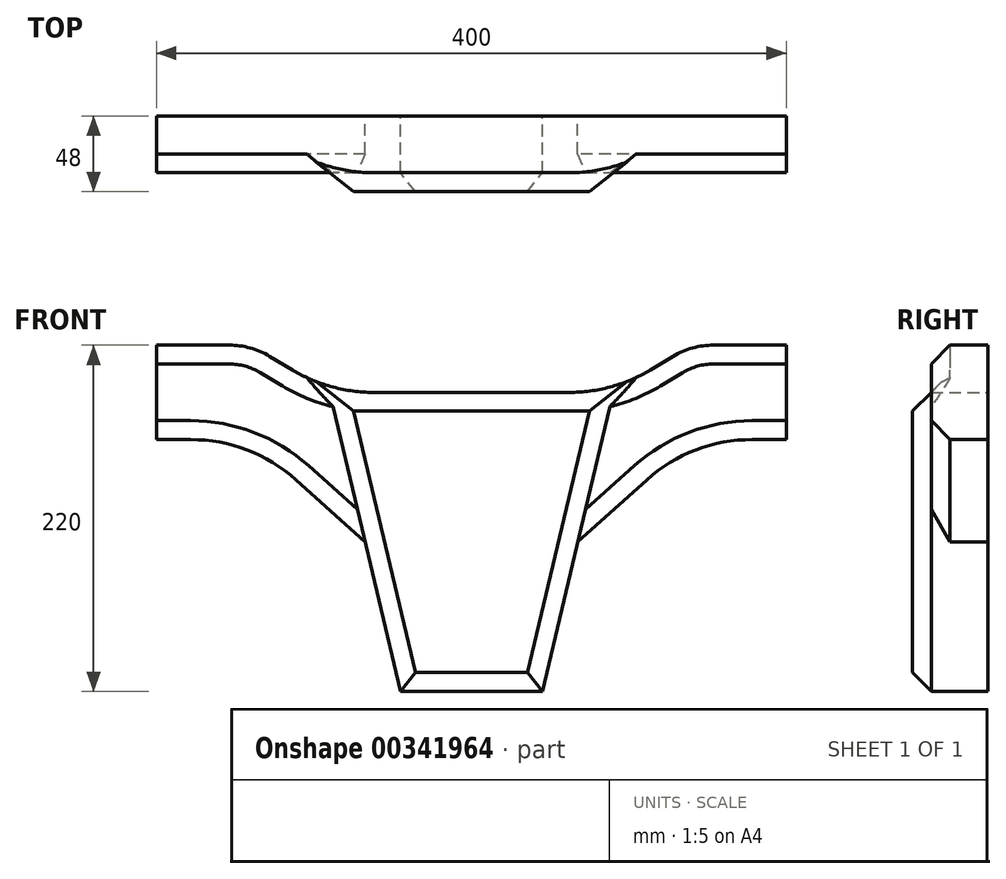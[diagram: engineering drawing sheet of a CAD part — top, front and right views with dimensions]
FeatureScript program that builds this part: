
annotation { "Feature Type Name" : "Feature", "Feature Type Description" : "" }
export const myFeature = defineFeature(function(context is Context, id is Id, definition is map)
    precondition{}
    {
        {
            var Q0;
            Q0=qCreatedBy(makeId("Front.planeOp"),FACE);
            var sketch = newSketch(context, id + "F0", { "sketchPlane" : qUnion([Q0])});
            skLineSegment(sketch, "E0", {"start": v(-45, -90) * mm, "end": v(45, -90) * mm});
            skLineSegment(sketch, "E1", {"start": v(-90, 100) * mm, "end": v(90, 100) * mm});
            skLineSegment(sketch, "E2", {"start": v(-45, -90) * mm, "end": v(-90, 100) * mm});
            skLineSegment(sketch, "E3", {"start": v(45, -90) * mm, "end": v(90, 100) * mm});
            skLineSegment(sketch, "E4", {"start": v(-200, 130) * mm, "end": v(-140, 130) * mm});
            skLineSegment(sketch, "E5", {"start": v(90, 100) * mm, "end": v(140, 130) * mm});
            skLineSegment(sketch, "E6.0", {"start": v(-200, 100) * mm, "end": v(200, 100) * mm, "construction": true});
            skLineSegment(sketch, "E7.0", {"start": v(-200, 70) * mm, "end": v(-140, 70) * mm});
            skLineSegment(sketch, "E8", {"start": v(67.5, 5) * mm, "end": v(140, 70) * mm});
            skLineSegment(sketch, "E9", {"start": v(-90, 100) * mm, "end": v(-140, 130) * mm});
            skLineSegment(sketch, "E10", {"start": v(-67.5, 5) * mm, "end": v(-140, 70) * mm});
            skLineSegment(sketch, "E11.trimOffspring", {"start": v(140, 70) * mm, "end": v(200, 70) * mm});
            skLineSegment(sketch, "E12", {"start": v(-200, 130) * mm, "end": v(-200, 70) * mm});
            skLineSegment(sketch, "E13", {"start": v(200, 130) * mm, "end": v(200, 70) * mm});
            skLineSegment(sketch, "E14.trimOffspring", {"start": v(140, 130) * mm, "end": v(200, 130) * mm});
            skSolve(sketch);
        }
        {
            var Q0;
            {var subQ3=sQuery(id+"F0.wireOp",EDGE,"E0");Q0=makeQuery(id+"F0.imprint","IMPRINT",FACE,{"disambiguationData":[TD([[makeQuery(id+"F0.imprint","IMPRINT",EDGE,{"derivedFrom":subQ3}),1.0]])]});}
            extrude(context, id + "F1", {"entities" : qUnion([Q0]), "depth" : 48 * mm});
        }
        {
            var Q0;
            {var subQ1=sQuery(id+"F0.wireOp",EDGE,"E5");Q0=makeQuery(id+"F0.imprint","IMPRINT",FACE,{"disambiguationData":[TD([[makeQuery(id+"F0.imprint","IMPRINT",EDGE,{"derivedFrom":subQ1}),-1.0]])]});}
            var Q1;
            Q1=makeQuery(id+"F0.imprint","IMPRINT",FACE,{"disambiguationData":[TD([[makeQuery(id+"F0.imprint","IMPRINT",EDGE,{"derivedFrom":sQuery(id+"F0.wireOp",EDGE,"E4")}),-1.0]])]});
            extrude(context, id + "F2", {"entities" : qUnion([Q0, Q1]), "operationType" : NewBodyOperationType.ADD, "depth" : 36 * mm});
        }
        {
            var Q0;
            {var subQ0=sQuery(id+"F0.wireOp",EDGE,"E9");var subQ1=sQuery(id+"F0.wireOp",EDGE,"E2");var subQ2=sQuery(id+"F0.wireOp",EDGE,"E1");Q0=makeQuery(id+"F2.boolean.opBoolean","MERGE",EDGE,{"derivedFrom":[makeQuery(id+"F1.opExtrude","SWEPT_EDGE",EDGE,{"disambiguationData":[OSD([subQ2,subQ1,subQ0])]}),makeQuery(id+"F2.opExtrude","SWEPT_EDGE",EDGE,{"disambiguationData":[OSD([subQ2,subQ1,subQ0])]})]});}
            var Q1;
            {var subQ0=sQuery(id+"F0.wireOp",EDGE,"E5");var subQ1=sQuery(id+"F0.wireOp",EDGE,"E3");var subQ2=sQuery(id+"F0.wireOp",EDGE,"E1");Q1=makeQuery(id+"F2.boolean.opBoolean","MERGE",EDGE,{"derivedFrom":[makeQuery(id+"F1.opExtrude","SWEPT_EDGE",EDGE,{"disambiguationData":[OSD([subQ2,subQ1,subQ0])]}),makeQuery(id+"F2.opExtrude","SWEPT_EDGE",EDGE,{"disambiguationData":[OSD([subQ2,subQ1,subQ0])]})]});}
            var Q2;
            Q2=makeQuery(id+"F2.opExtrude","SWEPT_EDGE",EDGE,{"disambiguationData":[OSD([sQuery(id+"F0.wireOp",EDGE,"E7.0"),sQuery(id+"F0.wireOp",EDGE,"E10")])]});
            var Q3;
            Q3=makeQuery(id+"F2.opExtrude","SWEPT_EDGE",EDGE,{"disambiguationData":[OSD([sQuery(id+"F0.wireOp",EDGE,"E8"),sQuery(id+"F0.wireOp",EDGE,"E11.trimOffspring")])]});
            fillet(context, id + "F3", {"entities" : qUnion([Q0, Q1, Q2, Q3]), "radius" : 100 * mm, "tangentPropagation" : true, "allowEdgeOverflow" : false});
        }
        {
            var Q0;
            Q0=makeQuery(id+"F2.opExtrude","SWEPT_EDGE",EDGE,{"disambiguationData":[OSD([sQuery(id+"F0.wireOp",EDGE,"E4"),sQuery(id+"F0.wireOp",EDGE,"E9")])]});
            var Q1;
            Q1=makeQuery(id+"F2.opExtrude","SWEPT_EDGE",EDGE,{"disambiguationData":[OSD([sQuery(id+"F0.wireOp",EDGE,"E5"),sQuery(id+"F0.wireOp",EDGE,"E14.trimOffspring")])]});
            fillet(context, id + "F4", {"entities" : qUnion([Q0, Q1]), "radius" : 50 * mm, "tangentPropagation" : true, "allowEdgeOverflow" : false});
        }
        {
            var Q0;
            Q0=makeQuery(id+"F1.opExtrude","CAP_EDGE",EDGE,{"disambiguationData":[OSD([sQuery(id+"F0.wireOp",EDGE,"E1")])],"isStart":false});
            var Q1;
            Q1=makeQuery(id+"F1.opExtrude","CAP_EDGE",EDGE,{"disambiguationData":[OSD([sQuery(id+"F0.wireOp",EDGE,"E2")])],"isStart":false});
            var Q2;
            Q2=makeQuery(id+"F1.opExtrude","CAP_EDGE",EDGE,{"disambiguationData":[OSD([sQuery(id+"F0.wireOp",EDGE,"E3")])],"isStart":false});
            var Q3;
            Q3=makeQuery(id+"F1.opExtrude","CAP_EDGE",EDGE,{"disambiguationData":[OSD([sQuery(id+"F0.wireOp",EDGE,"E0")])],"isStart":false});
            chamfer(context, id + "F5", {"entities" : qUnion([Q0, Q1, Q2, Q3]), "width" : 12 * mm, "tangentPropagation" : true});
        }
        {
            var Q0;
            {var subQ0=sQuery(id+"F0.wireOp",EDGE,"E5");var subQ1=sQuery(id+"F0.wireOp",EDGE,"E3");var subQ2=sQuery(id+"F0.wireOp",EDGE,"E1");Q0=makeQuery(id+"F3.opFillet","BLEND_EDGE",EDGE,{"blendedFrom":[makeQuery(id+"F2.boolean.opBoolean","MERGE",EDGE,{"derivedFrom":[makeQuery(id+"F1.opExtrude","SWEPT_EDGE",EDGE,{"disambiguationData":[OSD([subQ2,subQ1,subQ0])]}),makeQuery(id+"F2.opExtrude","SWEPT_EDGE",EDGE,{"disambiguationData":[OSD([subQ2,subQ1,subQ0])]})]}),makeQuery(id+"F2.opExtrude","CAP_FACE",FACE,{"disambiguationData":[OSD([subQ1,subQ0,sQuery(id+"F0.wireOp",EDGE,"E8"),sQuery(id+"F0.wireOp",EDGE,"E11.trimOffspring"),sQuery(id+"F0.wireOp",EDGE,"E13"),sQuery(id+"F0.wireOp",EDGE,"E14.trimOffspring")])],"isStart":false})],"blendedInto":[makeQuery(id+"F2.opExtrude","CAP_FACE",FACE,{"disambiguationData":[OSD([subQ1,subQ0,sQuery(id+"F0.wireOp",EDGE,"E8"),sQuery(id+"F0.wireOp",EDGE,"E11.trimOffspring"),sQuery(id+"F0.wireOp",EDGE,"E13"),sQuery(id+"F0.wireOp",EDGE,"E14.trimOffspring")])],"isStart":false})]});}
            var Q1;
            Q1=makeQuery(id+"F2.opExtrude","CAP_EDGE",EDGE,{"disambiguationData":[OSD([sQuery(id+"F0.wireOp",EDGE,"E4")])],"isStart":false});
            var Q2;
            {var subQ0=sQuery(id+"F0.wireOp",EDGE,"E10");var subQ1=sQuery(id+"F0.wireOp",EDGE,"E7.0");Q2=makeQuery(id+"F3.opFillet","BLEND_EDGE",EDGE,{"blendedFrom":[makeQuery(id+"F2.opExtrude","SWEPT_EDGE",EDGE,{"disambiguationData":[OSD([subQ1,subQ0])]}),makeQuery(id+"F2.opExtrude","CAP_FACE",FACE,{"disambiguationData":[OSD([sQuery(id+"F0.wireOp",EDGE,"E2"),sQuery(id+"F0.wireOp",EDGE,"E4"),subQ1,sQuery(id+"F0.wireOp",EDGE,"E9"),subQ0,sQuery(id+"F0.wireOp",EDGE,"E12")])],"isStart":false})],"blendedInto":[makeQuery(id+"F2.opExtrude","CAP_FACE",FACE,{"disambiguationData":[OSD([sQuery(id+"F0.wireOp",EDGE,"E2"),sQuery(id+"F0.wireOp",EDGE,"E4"),subQ1,sQuery(id+"F0.wireOp",EDGE,"E9"),subQ0,sQuery(id+"F0.wireOp",EDGE,"E12")])],"isStart":false})]});}
            var Q3;
            {var subQ0=sQuery(id+"F0.wireOp",EDGE,"E11.trimOffspring");var subQ1=sQuery(id+"F0.wireOp",EDGE,"E8");Q3=makeQuery(id+"F3.opFillet","BLEND_EDGE",EDGE,{"blendedFrom":[makeQuery(id+"F2.opExtrude","SWEPT_EDGE",EDGE,{"disambiguationData":[OSD([subQ1,subQ0])]}),makeQuery(id+"F2.opExtrude","CAP_FACE",FACE,{"disambiguationData":[OSD([sQuery(id+"F0.wireOp",EDGE,"E3"),sQuery(id+"F0.wireOp",EDGE,"E5"),subQ1,subQ0,sQuery(id+"F0.wireOp",EDGE,"E13"),sQuery(id+"F0.wireOp",EDGE,"E14.trimOffspring")])],"isStart":false})],"blendedInto":[makeQuery(id+"F2.opExtrude","CAP_FACE",FACE,{"disambiguationData":[OSD([sQuery(id+"F0.wireOp",EDGE,"E3"),sQuery(id+"F0.wireOp",EDGE,"E5"),subQ1,subQ0,sQuery(id+"F0.wireOp",EDGE,"E13"),sQuery(id+"F0.wireOp",EDGE,"E14.trimOffspring")])],"isStart":false})]});}
            chamfer(context, id + "F6", {"entities" : qUnion([Q0, Q1, Q2, Q3]), "width" : 12 * mm, "tangentPropagation" : true});
        }
    });
